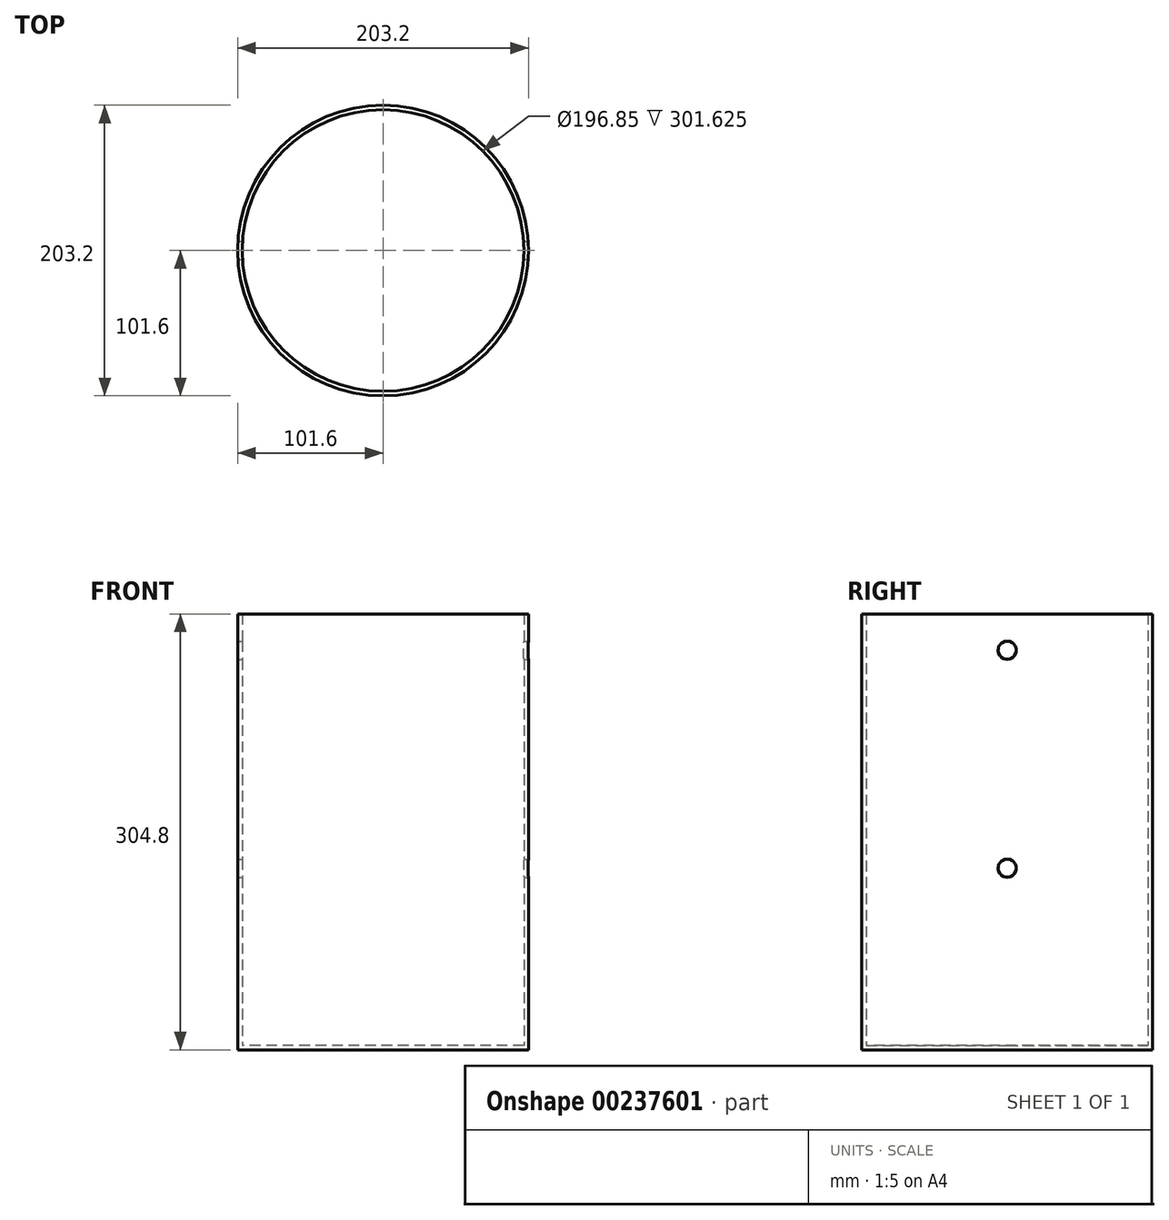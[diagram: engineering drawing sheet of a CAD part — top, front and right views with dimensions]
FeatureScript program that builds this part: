
annotation { "Feature Type Name" : "Feature", "Feature Type Description" : "" }
export const myFeature = defineFeature(function(context is Context, id is Id, definition is map)
    precondition{}
    {
        {
            var Q0;
            Q0=qCreatedBy(makeId("Top.planeOp"),FACE);
            var sketch = newSketch(context, id + "F0", { "sketchPlane" : qUnion([Q0])});
            skCircle(sketch, "E0", {"center": v(0, 0) * mm, "radius": 101.6 * mm});
            skSolve(sketch);
        }
        {
            var Q0;
            Q0=makeQuery(id+"F0.imprint","IMPRINT",FACE,{"disambiguationData":[TD([[makeQuery(id+"F0.imprint","IMPRINT",EDGE,{"derivedFrom":sQuery(id+"F0.wireOp",EDGE,"E0")}),1.0]])]});
            extrude(context, id + "F1", {"entities" : qUnion([Q0]), "depth" : 304.8 * mm});
        }
        {
            var Q0;
            Q0=makeQuery(id+"F1.opExtrude","CAP_FACE",FACE,{"disambiguationData":[OSD([sQuery(id+"F0.wireOp",EDGE,"E0")])],"isStart":false});
            shell(context, id + "F2", {"entities" : qUnion([Q0]), "thickness" : 3.17 * mm});
        }
        {
            var Q0;
            Q0=qCreatedBy(makeId("Right.planeOp"),FACE);
            var sketch = newSketch(context, id + "F3", { "sketchPlane" : qUnion([Q0])});
            skCircle(sketch, "E1", {"center": v(0, 279.4) * mm, "radius": 6.35 * mm});
            skCircle(sketch, "E2", {"center": v(0, 127) * mm, "radius": 6.35 * mm});
            skSolve(sketch);
        }
        {
            var Q0;
            Q0=makeQuery(id+"F3.imprint","IMPRINT",FACE,{"disambiguationData":[TD([[makeQuery(id+"F3.imprint","IMPRINT",EDGE,{"derivedFrom":sQuery(id+"F3.wireOp",EDGE,"E1")}),1.0]])]});
            var Q1;
            Q1=makeQuery(id+"F3.imprint","IMPRINT",FACE,{"disambiguationData":[TD([[makeQuery(id+"F3.imprint","IMPRINT",EDGE,{"derivedFrom":sQuery(id+"F3.wireOp",EDGE,"E2")}),1.0]])]});
            extrude(context, id + "F4", {"entities" : qUnion([Q0, Q1]), "operationType" : NewBodyOperationType.REMOVE, "endBound" : BoundingType.SYMMETRIC, "oppositeDirection" : true, "depth" : 558.8 * mm});
        }
    });
